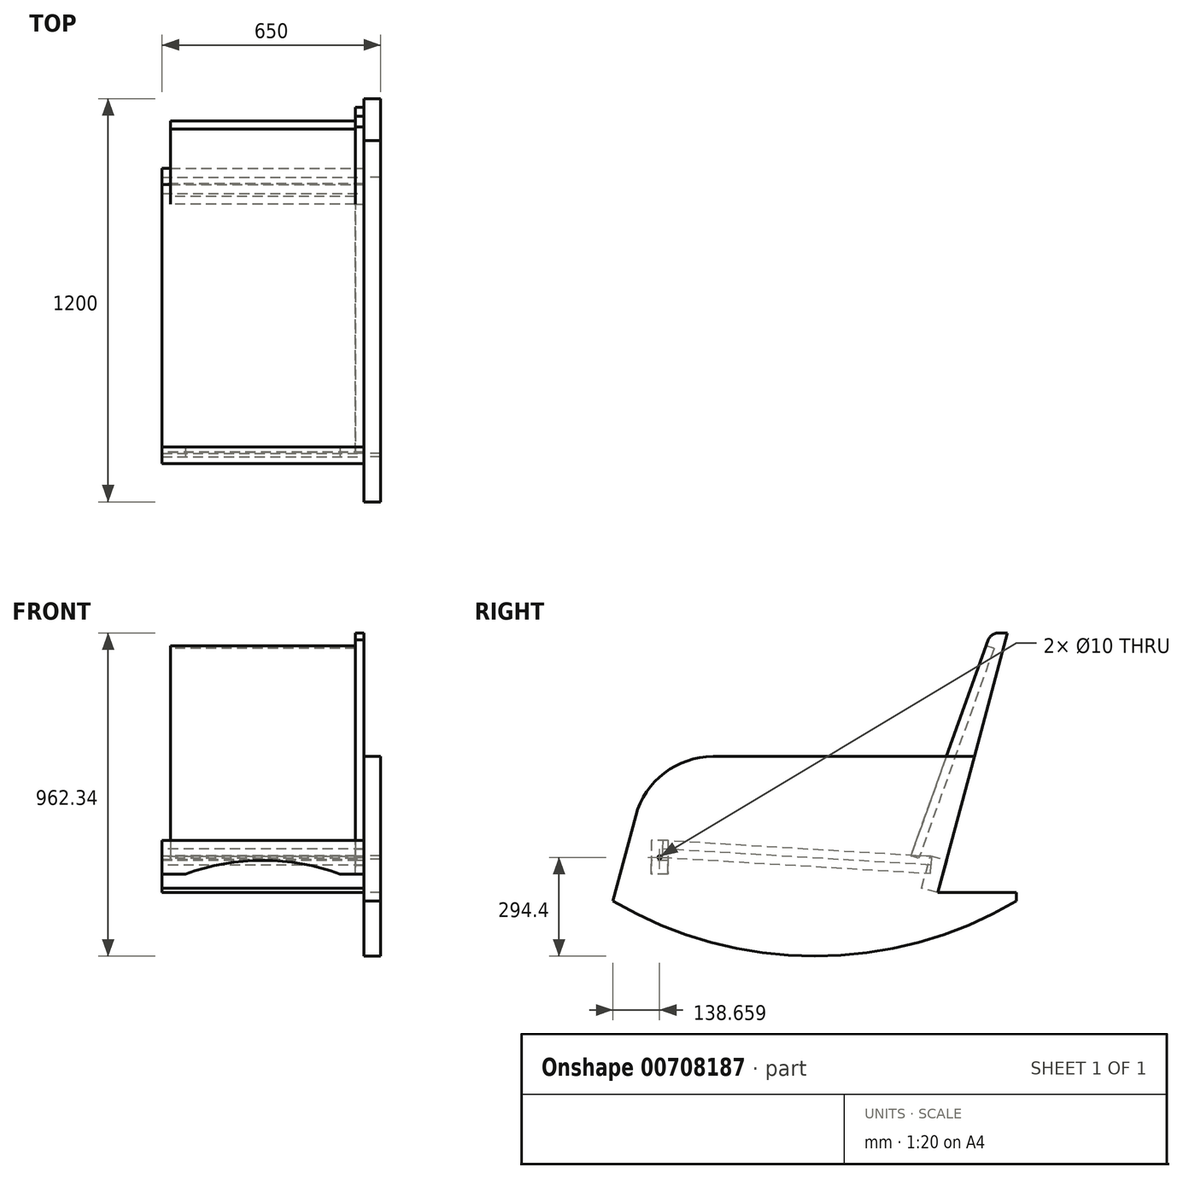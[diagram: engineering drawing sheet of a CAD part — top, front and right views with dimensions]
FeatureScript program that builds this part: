
annotation { "Feature Type Name" : "Feature", "Feature Type Description" : "" }
export const myFeature = defineFeature(function(context is Context, id is Id, definition is map)
    precondition{}
    {
        {
            var Q0;
            Q0=qCreatedBy(makeId("Right.planeOp"),FACE);
            var sketch = newSketch(context, id + "F0", { "sketchPlane" : qUnion([Q0])});
            skLineSegment(sketch, "E0.bottom", {"start": v(-600, 300) * mm, "end": v(600, 300) * mm});
            skLineSegment(sketch, "E0.top", {"start": v(-600, -300) * mm, "end": v(600, -300) * mm});
            skLineSegment(sketch, "E0.left", {"start": v(-600, 300) * mm, "end": v(-600, -300) * mm});
            skLineSegment(sketch, "E0.right", {"start": v(600, 300) * mm, "end": v(600, -300) * mm});
            skPoint(sketch, "E0.middle", {"position": v(0, 0) * mm});
            skArc(sketch, "E1", {"start": v(-600, -130) * mm, "mid": v(0, -294.4) * mm, "end": v(600, -130) * mm});
            skLineSegment(sketch, "E2.top", {"start": v(600, 300) * mm, "end": v(350, 300) * mm});
            skLineSegment(sketch, "E3.left", {"start": v(600, 0) * mm, "end": v(600, 300) * mm});
            skLineSegment(sketch, "E4.bottom", {"start": v(350, 300) * mm, "end": v(600, 300) * mm});
            skLineSegment(sketch, "E4.top", {"start": v(366.54, -104.8) * mm, "end": v(600, -104.8) * mm});
            skLineSegment(sketch, "E4.right", {"start": v(600, 300) * mm, "end": v(600, -104.8) * mm});
            skLineSegment(sketch, "E5", {"start": v(-600, -130) * mm, "end": v(-484.78, 300) * mm});
            skLineSegment(sketch, "E6", {"start": v(-484.78, 300) * mm, "end": v(-600, 300) * mm});
            skCircle(sketch, "E7", {"center": v(-461.34, 0) * mm, "radius": 5 * mm});
            skLineSegment(sketch, "E8", {"start": v(366.54, -104.8) * mm, "end": v(475, 300) * mm});
            skArc(sketch, "E9", {"start": v(-302.25, 300) * mm, "mid": v(-447.06, 250.84) * mm, "end": v(-532.02, 123.7) * mm});
            skSolve(sketch);
        }
        {
            var Q0;
            {var subQ4=sQuery(id+"F0.wireOp",EDGE,"E1");Q0=makeQuery(id+"F0.imprint","IMPRINT",FACE,{"disambiguationData":[TD([[makeQuery(id+"F0.imprint","IMPRINT",EDGE,{"derivedFrom":subQ4}),1.0]])]});}
            extrude(context, id + "F1", {"entities" : qUnion([Q0]), "depth" : 50 * mm, "offsetDistance" : 25 * mm});
        }
        {
            var Q0;
            Q0=makeQuery(id+"F1.opExtrude","CAP_FACE",FACE,{"disambiguationData":[OSD([sQuery(id+"F0.wireOp",EDGE,"E0.bottom"),sQuery(id+"F0.wireOp",EDGE,"E0.right"),sQuery(id+"F0.wireOp",EDGE,"E1"),sQuery(id+"F0.wireOp",EDGE,"E4.top"),sQuery(id+"F0.wireOp",EDGE,"E4.left"),sQuery(id+"F0.wireOp",EDGE,"E5"),sQuery(id+"F0.wireOp",EDGE,"E7")])],"isStart":true});
            var sketch = newSketch(context, id + "F2", { "sketchPlane" : qUnion([Q0])});
            skLineSegment(sketch, "E10.bottom", {"start": v(436.34, 50) * mm, "end": v(486.34, 50) * mm});
            skLineSegment(sketch, "E10.top", {"start": v(436.34, -50) * mm, "end": v(486.34, -50) * mm});
            skLineSegment(sketch, "E10.left", {"start": v(436.34, 50) * mm, "end": v(436.34, -50) * mm});
            skLineSegment(sketch, "E10.right", {"start": v(486.34, 50) * mm, "end": v(486.34, -50) * mm});
            skPoint(sketch, "E10.middle", {"position": v(461.34, 0) * mm});
            skPoint(sketch, "E11", {"position": v(436.34, 25) * mm});
            skSolve(sketch);
        }
        {
            var Q0;
            Q0=makeQuery(id+"F2.imprint","IMPRINT",FACE,{"disambiguationData":[TD([[makeQuery(id+"F2.imprint","IMPRINT",EDGE,{"derivedFrom":sQuery(id+"F2.wireOp",EDGE,"E10.bottom")}),-1.0]])]});
            extrude(context, id + "F3", {"entities" : qUnion([Q0]), "depth" : 600 * mm, "offsetDistance" : 25 * mm});
        }
        {
            var Q0;
            Q0=makeQuery(id+"F1.opExtrude","CAP_FACE",FACE,{"disambiguationData":[OSD([sQuery(id+"F0.wireOp",EDGE,"E0.bottom"),sQuery(id+"F0.wireOp",EDGE,"E0.right"),sQuery(id+"F0.wireOp",EDGE,"E1"),sQuery(id+"F0.wireOp",EDGE,"E4.top"),sQuery(id+"F0.wireOp",EDGE,"E4.left"),sQuery(id+"F0.wireOp",EDGE,"E5"),sQuery(id+"F0.wireOp",EDGE,"E7")])],"isStart":true});
            var sketch = newSketch(context, id + "F4", { "sketchPlane" : qUnion([Q0])});
            skLineSegment(sketch, "E12", {"start": v(-366.54, -104.8) * mm, "end": v(-318.24, -91.86) * mm});
            skLineSegment(sketch, "E13", {"start": v(-318.24, -91.86) * mm, "end": v(-344.12, 4.74) * mm});
            skLineSegment(sketch, "E14", {"start": v(-344.12, 4.74) * mm, "end": v(-392.42, -8.2) * mm});
            skLineSegment(sketch, "E15", {"start": v(-392.42, -8.2) * mm, "end": v(-366.54, -104.8) * mm});
            skSolve(sketch);
        }
        {
            var Q0;
            Q0 = qSketchRegion(id + "F4", true);
            extrude(context, id + "F5", {"entities" : qUnion([Q0]), "depth" : 600 * mm, "offsetDistance" : 25 * mm});
        }
        {
            var Q0;
            Q0=makeQuery(id+"F1.opExtrude","CAP_FACE",FACE,{"disambiguationData":[OSD([sQuery(id+"F0.wireOp",EDGE,"E0.bottom"),sQuery(id+"F0.wireOp",EDGE,"E0.right"),sQuery(id+"F0.wireOp",EDGE,"E1"),sQuery(id+"F0.wireOp",EDGE,"E4.bottom"),sQuery(id+"F0.wireOp",EDGE,"E4.top"),sQuery(id+"F0.wireOp",EDGE,"E5"),sQuery(id+"F0.wireOp",EDGE,"E7"),sQuery(id+"F0.wireOp",EDGE,"E8")])],"isStart":true});
            var sketch = newSketch(context, id + "F6", { "sketchPlane" : qUnion([Q0])});
            skLineSegment(sketch, "E16", {"start": v(-392.42, -8.2) * mm, "end": v(-573.6, 667.94) * mm});
            skLineSegment(sketch, "E17", {"start": v(-285.85, 4.74) * mm, "end": v(-344.12, 4.74) * mm});
            skLineSegment(sketch, "E18", {"start": v(-344.12, 4.74) * mm, "end": v(-392.42, -8.2) * mm});
            skLineSegment(sketch, "E19", {"start": v(-573.6, 667.94) * mm, "end": v(-523.6, 667.94) * mm});
            skLineSegment(sketch, "E20", {"start": v(-523.6, 667.94) * mm, "end": v(-285.85, 4.74) * mm});
            skArc(sketch, "E21", {"start": v(-516.22, 647.4) * mm, "mid": v(-529.35, 662.48) * mm, "end": v(-548.6, 667.94) * mm});
            skSolve(sketch);
        }
        {
            var Q0;
            {var subQ3=sQuery(id+"F6.wireOp",EDGE,"E19");Q0=makeQuery(id+"F6.imprint","IMPRINT",FACE,{"disambiguationData":[TD([[makeQuery(id+"F6.imprint","IMPRINT",EDGE,{"derivedFrom":subQ3}),-1.0]])]});}
            var Q1;
            {var subQ1=sQuery(id+"F6.wireOp",EDGE,"E17");Q1=makeQuery(id+"F6.imprint","IMPRINT",FACE,{"disambiguationData":[TD([[makeQuery(id+"F6.imprint","IMPRINT",EDGE,{"derivedFrom":subQ1}),-1.0]])]});}
            extrude(context, id + "F7", {"entities" : qUnion([Q0, Q1]), "depth" : 25 * mm, "offsetDistance" : 25 * mm});
        }
        {
            var Q0;
            Q0=makeQuery(id+"F1.opExtrude","CAP_FACE",FACE,{"disambiguationData":[OSD([sQuery(id+"F0.wireOp",EDGE,"E0.bottom"),sQuery(id+"F0.wireOp",EDGE,"E0.right"),sQuery(id+"F0.wireOp",EDGE,"E1"),sQuery(id+"F0.wireOp",EDGE,"E4.bottom"),sQuery(id+"F0.wireOp",EDGE,"E4.top"),sQuery(id+"F0.wireOp",EDGE,"E5"),sQuery(id+"F0.wireOp",EDGE,"E7"),sQuery(id+"F0.wireOp",EDGE,"E8")])],"isStart":true});
            var sketch = newSketch(context, id + "F8", { "sketchPlane" : qUnion([Q0])});
            skLineSegment(sketch, "E22", {"start": v(454.55, 0) * mm, "end": v(-344.03, -47.72) * mm});
            skLineSegment(sketch, "E23", {"start": v(-344.03, -47.72) * mm, "end": v(-345.52, -22.77) * mm});
            skLineSegment(sketch, "E24", {"start": v(-345.52, -22.77) * mm, "end": v(453.06, 24.96) * mm});
            skLineSegment(sketch, "E25", {"start": v(453.06, 24.96) * mm, "end": v(454.55, 0) * mm});
            skSolve(sketch);
        }
        {
            var Q0;
            Q0=makeQuery(id+"F8.imprint","IMPRINT",FACE,{"disambiguationData":[TD([[makeQuery(id+"F8.imprint","IMPRINT",EDGE,{"derivedFrom":sQuery(id+"F8.wireOp",EDGE,"E22")}),-1.0]])]});
            extrude(context, id + "F9", {"entities" : qUnion([Q0]), "depth" : 25 * mm, "offsetDistance" : 25 * mm});
        }
        {
            var Q0;
            Q0=makeQuery(id+"F9.opExtrude","SWEPT_FACE",FACE,{"disambiguationData":[OSD([sQuery(id+"F8.wireOp",EDGE,"E24")])]});
            var sketch = newSketch(context, id + "F10", { "sketchPlane" : qUnion([Q0])});
            skLineSegment(sketch, "E26.bottom", {"start": v(0, 346.26) * mm, "end": v(-600, 346.26) * mm});
            skLineSegment(sketch, "E26.top", {"start": v(0, -453.74) * mm, "end": v(-600, -453.74) * mm});
            skLineSegment(sketch, "E26.left", {"start": v(0, 346.26) * mm, "end": v(0, -453.74) * mm});
            skLineSegment(sketch, "E26.right", {"start": v(-600, 346.26) * mm, "end": v(-600, -453.74) * mm});
            skSolve(sketch);
        }
        {
            var Q0;
            Q0 = qSketchRegion(id + "F10", true);
            extrude(context, id + "F11", {"entities" : qUnion([Q0]), "depth" : 25 * mm, "offsetDistance" : 25 * mm});
        }
        {
            var Q0;
            Q0=makeQuery(id+"F7.opExtrude","SWEPT_FACE",FACE,{"disambiguationData":[OSD([sQuery(id+"F6.wireOp",EDGE,"E20")])]});
            var sketch = newSketch(context, id + "F12", { "sketchPlane" : qUnion([Q0])});
            skLineSegment(sketch, "E27.bottom", {"start": v(0, 765.1) * mm, "end": v(-575, 765.1) * mm});
            skLineSegment(sketch, "E27.top", {"start": v(0, 100.92) * mm, "end": v(-575, 100.92) * mm});
            skLineSegment(sketch, "E27.left", {"start": v(0, 765.1) * mm, "end": v(0, 100.92) * mm});
            skLineSegment(sketch, "E27.right", {"start": v(-575, 765.1) * mm, "end": v(-575, 100.92) * mm});
            skSolve(sketch);
        }
        {
            var Q0;
            {var subQ0=sQuery(id+"F12.wireOp",EDGE,"E27.right");Q0=makeQuery(id+"F12.imprint","IMPRINT",FACE,{"disambiguationData":[TD([[makeQuery(id+"F12.imprint","IMPRINT",EDGE,{"derivedFrom":subQ0}),1.0]])]});}
            extrude(context, id + "F13", {"entities" : qUnion([Q0]), "oppositeDirection" : true, "depth" : 25 * mm, "offsetDistance" : 25 * mm});
        }
        {
            var Q0;
            Q0=makeQuery(id+"F3.opExtrude","SWEPT_FACE",FACE,{"disambiguationData":[OSD([sQuery(id+"F2.wireOp",EDGE,"E10.right")])]});
            var sketch = newSketch(context, id + "F14", { "sketchPlane" : qUnion([Q0])});
            skArc(sketch, "E28", {"start": v(-70, -50) * mm, "mid": v(-300, -9) * mm, "end": v(-530, -50) * mm});
            skSolve(sketch);
        }
        {
            var Q0;
            {var subQ0=sQuery(id+"F14.wireOp",EDGE,"E28");Q0=makeQuery(id+"F14.imprint","IMPRINT",FACE,{"disambiguationData":[TD([[makeQuery(id+"F14.imprint","IMPRINT",EDGE,{"derivedFrom":subQ0}),1.0]])]});}
            extrude(context, id + "F15", {"entities" : qUnion([Q0]), "operationType" : NewBodyOperationType.REMOVE, "oppositeDirection" : true, "depth" : 50 * mm, "offsetDistance" : 25 * mm});
        }
    });
